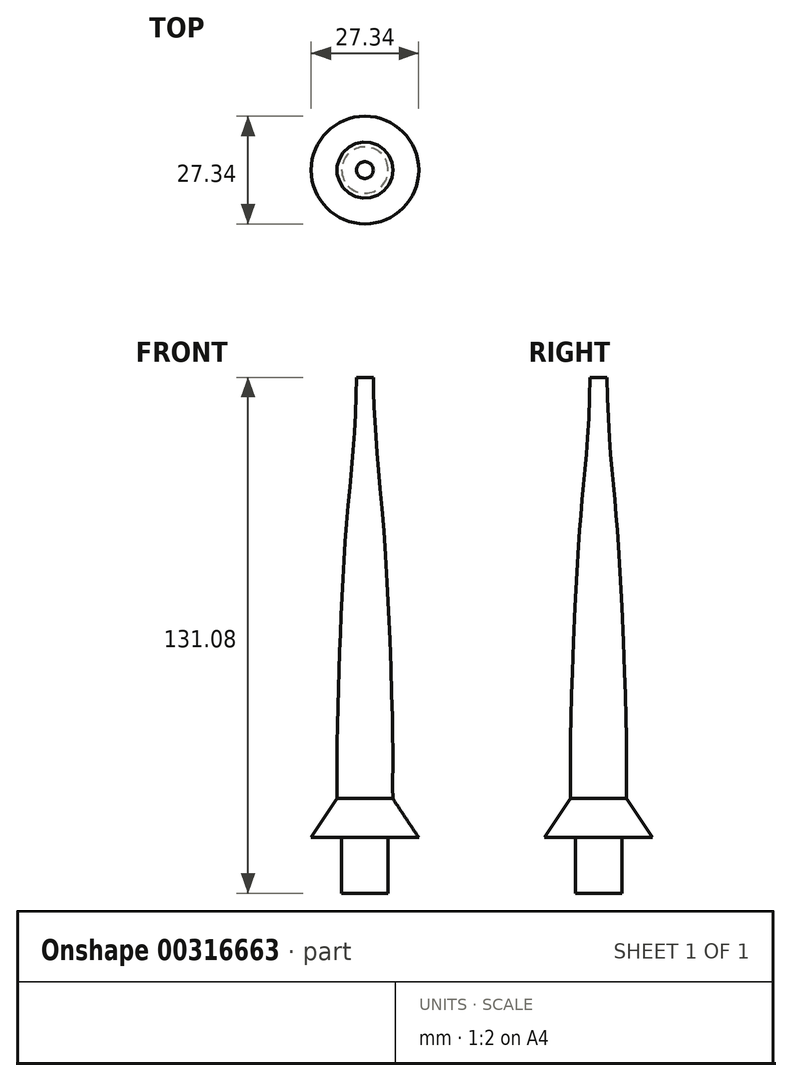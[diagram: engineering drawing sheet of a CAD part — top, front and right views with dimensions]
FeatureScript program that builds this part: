
annotation { "Feature Type Name" : "Feature", "Feature Type Description" : "" }
export const myFeature = defineFeature(function(context is Context, id is Id, definition is map)
    precondition{}
    {
        {
            var Q0;
            Q0=qCreatedBy(makeId("Front.planeOp"),FACE);
            var sketch = newSketch(context, id + "F0", { "sketchPlane" : qUnion([Q0])});
            skLineSegment(sketch, "E0", {"start": v(0, 76.53) * mm, "end": v(0, -76.95) * mm, "construction": true});
            skLineSegment(sketch, "E1", {"start": v(-5.9, -76.95) * mm, "end": v(-5.9, -62.8) * mm});
            skLineSegment(sketch, "E2", {"start": v(-5.9, -62.8) * mm, "end": v(-13.67, -62.8) * mm});
            skLineSegment(sketch, "E3", {"start": v(-13.67, -62.8) * mm, "end": v(-7.07, -52.9) * mm});
            skFitSpline(sketch, "E4", {"points": [v(-7.07, -52.9) * mm, v(-7.07, -45.6) * mm, v(-7.07, -37.58) * mm, v(-5.19, 9.57) * mm, v(-2.83, 38.1) * mm, v(-2.12, 54.13) * mm], "startDerivative": vector(0.18, 62.08) * mm, "endDerivative": vector(2.44, 84.1) * mm});
            skLineSegment(sketch, "E5", {"start": v(-2.12, 54.13) * mm, "end": v(0, 54.13) * mm});
            skLineSegment(sketch, "E6", {"start": v(0, 54.13) * mm, "end": v(0, -76.95) * mm});
            skLineSegment(sketch, "E7", {"start": v(-5.9, -76.95) * mm, "end": v(0, -76.95) * mm});
            skSolve(sketch);
        }
        {
            var Q0;
            Q0=makeQuery(id+"F0.imprint","IMPRINT",FACE,{"disambiguationData":[TD([[makeQuery(id+"F0.imprint","IMPRINT",EDGE,{"derivedFrom":sQuery(id+"F0.wireOp",EDGE,"E1")}),-1.0]])]});
            var Q1;
            Q1=sQuery(id+"F0.wireOp",EDGE,"E6");
            revolve(context, id + "F1", {"entities" : qUnion([Q0]), "axis" : qUnion([Q1]), "revolveType" : RevolveType.FULL});
        }
    });
